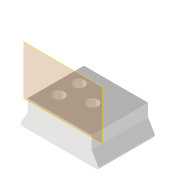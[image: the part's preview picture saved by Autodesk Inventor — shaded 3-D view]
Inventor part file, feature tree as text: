
AUTODESK INVENTOR PART (.ipt)
format: ipt  version: 2022 (Build 260153000, 153)  size: 137,728 bytes
history: native  units: mm
features: reference x7, other x3, plane x2, sketch x2, extrude x1, fillet x1, hole x1
ambient origin geometry x8: Origin, YZ Plane, XZ Plane, XY Plane, X Axis, Y Axis, Z Axis, Center Point
bodies: Volumenkörper1 (feature_tree)
feature tree (17):
  plane  "Arbeitsebene1"
  sketch  "Skizze1"  dims[d0=3.0mm d1=4.0mm d2=120.0deg]
  plane  "Arbeitsebene2"
  extrude  "Extrusion1"  Depth=3.0mm
  fillet  "Rundung1"  [1 undecoded]
  hole  "Bohrung1"  [1 undecoded]
  reference  "Referenz1"
  reference  "Referenz2"
  reference  "Referenz3"
  reference  "Referenz4"
  reference  "Referenz5"
  sketch  "Skizze2"  dims[d3=60.0deg d4=10.0mm d5=0.0mm d6=0.5mm d7=2.8mm d8=6.0mm d9=6.5mm d10=3.0mm d11=90.0deg d12=14.0mm d13=20.594885mm d14=2.0mm]
  reference  "Referenz6"
  reference  "Referenz7"
  other  "Assembly_Cassete_Deck.iam"
  other  "10_Cassette_microscopy_deck:1"
  other  "10_Base_puzzle_v3:3"
note: 2 required parameter values undecoded (feature->parameter linkage not recoverable at this tier; creation-order binding heuristic only, values carry confidence <= 0.55)
